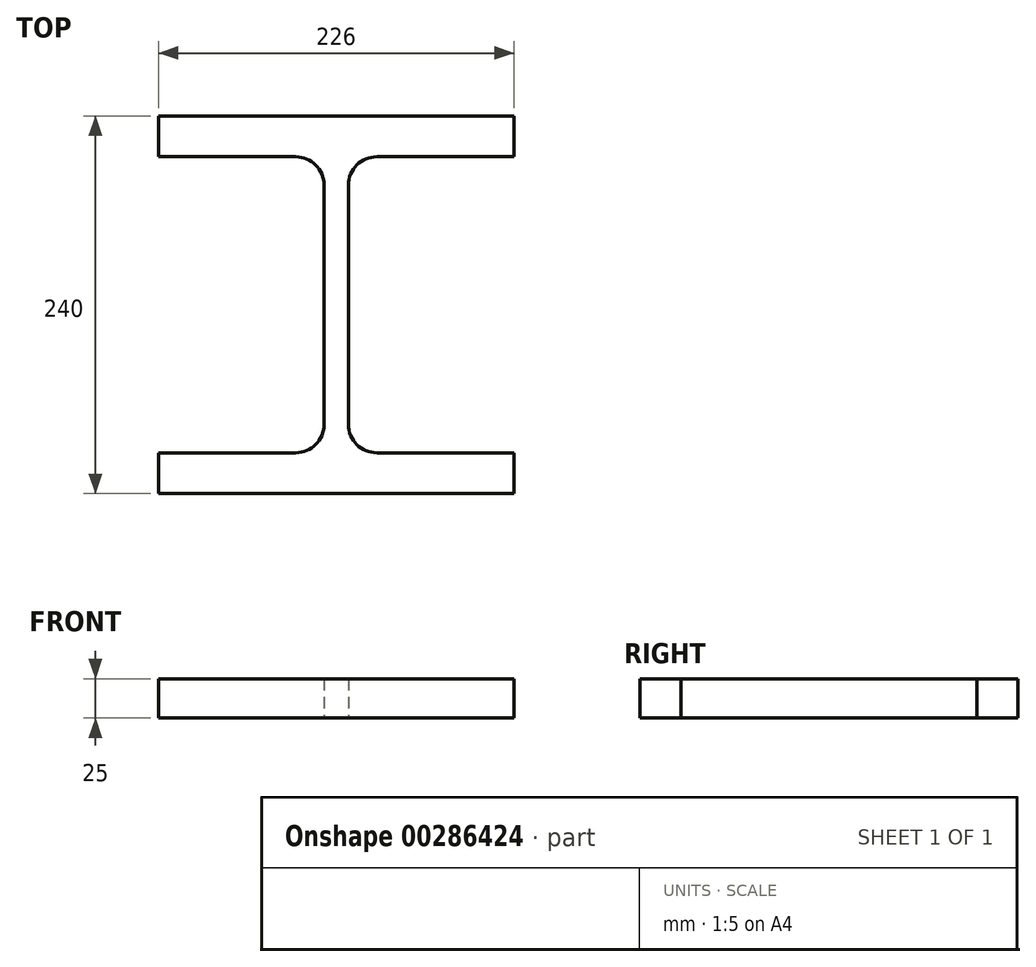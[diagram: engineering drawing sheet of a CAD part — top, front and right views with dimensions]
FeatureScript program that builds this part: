
annotation { "Feature Type Name" : "Feature", "Feature Type Description" : "" }
export const myFeature = defineFeature(function(context is Context, id is Id, definition is map)
    precondition{}
    {
        {
            var Q0;
            Q0=qCreatedBy(makeId("Top.planeOp"),FACE);
            var sketch = newSketch(context, id + "F0", { "sketchPlane" : qUnion([Q0])});
            skLineSegment(sketch, "E0", {"start": v(-114.7, 52.98) * mm, "end": v(111.3, 52.98) * mm});
            skLineSegment(sketch, "E1", {"start": v(-114.7, 52.98) * mm, "end": v(-114.7, 26.98) * mm});
            skLineSegment(sketch, "E2", {"start": v(111.3, 52.98) * mm, "end": v(111.3, 26.98) * mm});
            skLineSegment(sketch, "E3", {"start": v(-114.7, -161.02) * mm, "end": v(-114.7, -187.02) * mm});
            skLineSegment(sketch, "E4", {"start": v(111.3, -161.02) * mm, "end": v(111.3, -187.02) * mm});
            skLineSegment(sketch, "E5", {"start": v(-114.7, -187.02) * mm, "end": v(111.3, -187.02) * mm});
            skPoint(sketch, "E6.visualSharp", {"position": v(-17.2, 26.98) * mm});
            skPoint(sketch, "E7.visualSharp", {"position": v(13.8, 26.98) * mm});
            skPoint(sketch, "E8.visualSharp", {"position": v(13.8, -161.02) * mm});
            skPoint(sketch, "E9.visualSharp", {"position": v(-17.2, -161.02) * mm});
            skLineSegment(sketch, "E10", {"start": v(-114.7, 26.98) * mm, "end": v(-27.44, 26.98) * mm});
            skLineSegment(sketch, "E11", {"start": v(111.3, 26.98) * mm, "end": v(24.06, 26.98) * mm});
            skLineSegment(sketch, "E12", {"start": v(111.3, -161.02) * mm, "end": v(24.06, -161.02) * mm});
            skLineSegment(sketch, "E13", {"start": v(-114.7, -161.02) * mm, "end": v(-27.44, -161.02) * mm});
            skLineSegment(sketch, "E14", {"start": v(-9.44, 8.98) * mm, "end": v(-9.44, -143.02) * mm});
            skLineSegment(sketch, "E15", {"start": v(6.06, -143.02) * mm, "end": v(6.06, 8.98) * mm});
            skPoint(sketch, "E16.visualSharp", {"position": v(-9.44, 26.98) * mm});
            skArc(sketch, "E16.filletArc", {"start": v(-9.44, 8.98) * mm, "mid": v(-14.72, 21.7) * mm, "end": v(-27.44, 26.98) * mm});
            skPoint(sketch, "E17.visualSharp", {"position": v(6.06, 26.98) * mm});
            skArc(sketch, "E17.filletArc", {"start": v(24.06, 26.98) * mm, "mid": v(11.33, 21.7) * mm, "end": v(6.06, 8.98) * mm});
            skPoint(sketch, "E18.visualSharp", {"position": v(6.06, -161.02) * mm});
            skArc(sketch, "E18.filletArc", {"start": v(6.06, -143.02) * mm, "mid": v(11.33, -155.75) * mm, "end": v(24.06, -161.02) * mm});
            skPoint(sketch, "E19.visualSharp", {"position": v(-9.44, -161.02) * mm});
            skArc(sketch, "E19.filletArc", {"start": v(-27.44, -161.02) * mm, "mid": v(-14.72, -155.75) * mm, "end": v(-9.44, -143.02) * mm});
            skSolve(sketch);
        }
        {
            var Q0;
            Q0 = qSketchRegion(id + "F0", true);
            extrude(context, id + "F1", {"entities" : qUnion([Q0]), "depth" : 25 * mm});
        }
    });
